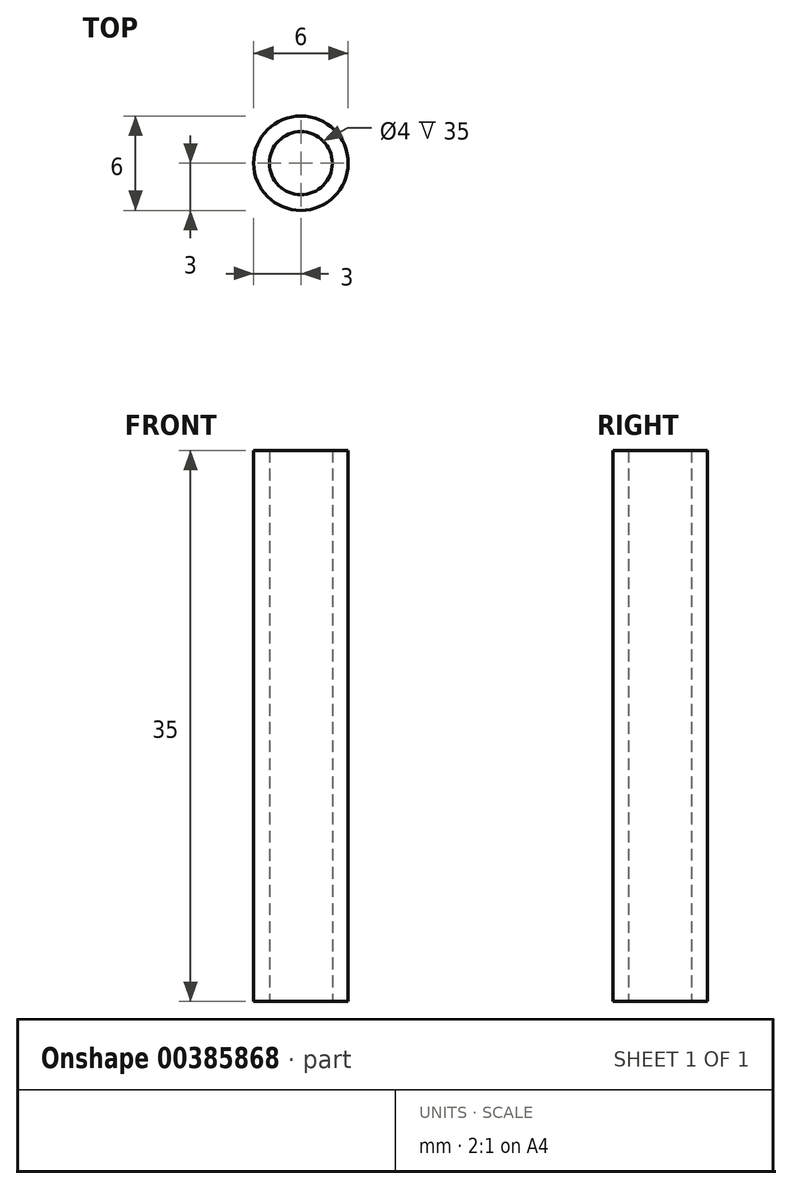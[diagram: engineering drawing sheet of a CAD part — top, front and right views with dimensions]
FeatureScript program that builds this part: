
annotation { "Feature Type Name" : "Feature", "Feature Type Description" : "" }
export const myFeature = defineFeature(function(context is Context, id is Id, definition is map)
    precondition{}
    {
        {
            var Q0;
            Q0=qCreatedBy(makeId("Top.planeOp"),FACE);
            var sketch = newSketch(context, id + "F0", { "sketchPlane" : qUnion([Q0])});
            skCircle(sketch, "E0", {"center": v(0, 0) * mm, "radius": 3 * mm});
            skSolve(sketch);
        }
        {
            var Q0;
            Q0 = qSketchRegion(id + "F0", true);
            extrude(context, id + "F1", {"entities" : qUnion([Q0]), "depth" : 35 * mm});
        }
        {
            var Q0;
            Q0=sQuery(id+"F0.wireOp",VERTEX,"E0.center");
            var Q1;
            Q1=makeQuery(id+"F1.opExtrude","SWEPT_BODY",BODY,{"disambiguationData":[OSD([sQuery(id+"F0.wireOp",EDGE,"E0")])]});
            hole(context, id + "F2", {"style" : HoleStyle.SIMPLE, "endStyle" : HoleEndStyle.THROUGH, "oppositeDirection" : true, "holeDiameter" : 4 * mm, "isTappedThrough" : true, "tappedDepth" : 12 * mm, "tapClearance" : 3, "startFromSketch" : true, "locations" : qUnion([Q0]), "scope" : qUnion([Q1])});
        }
    });
